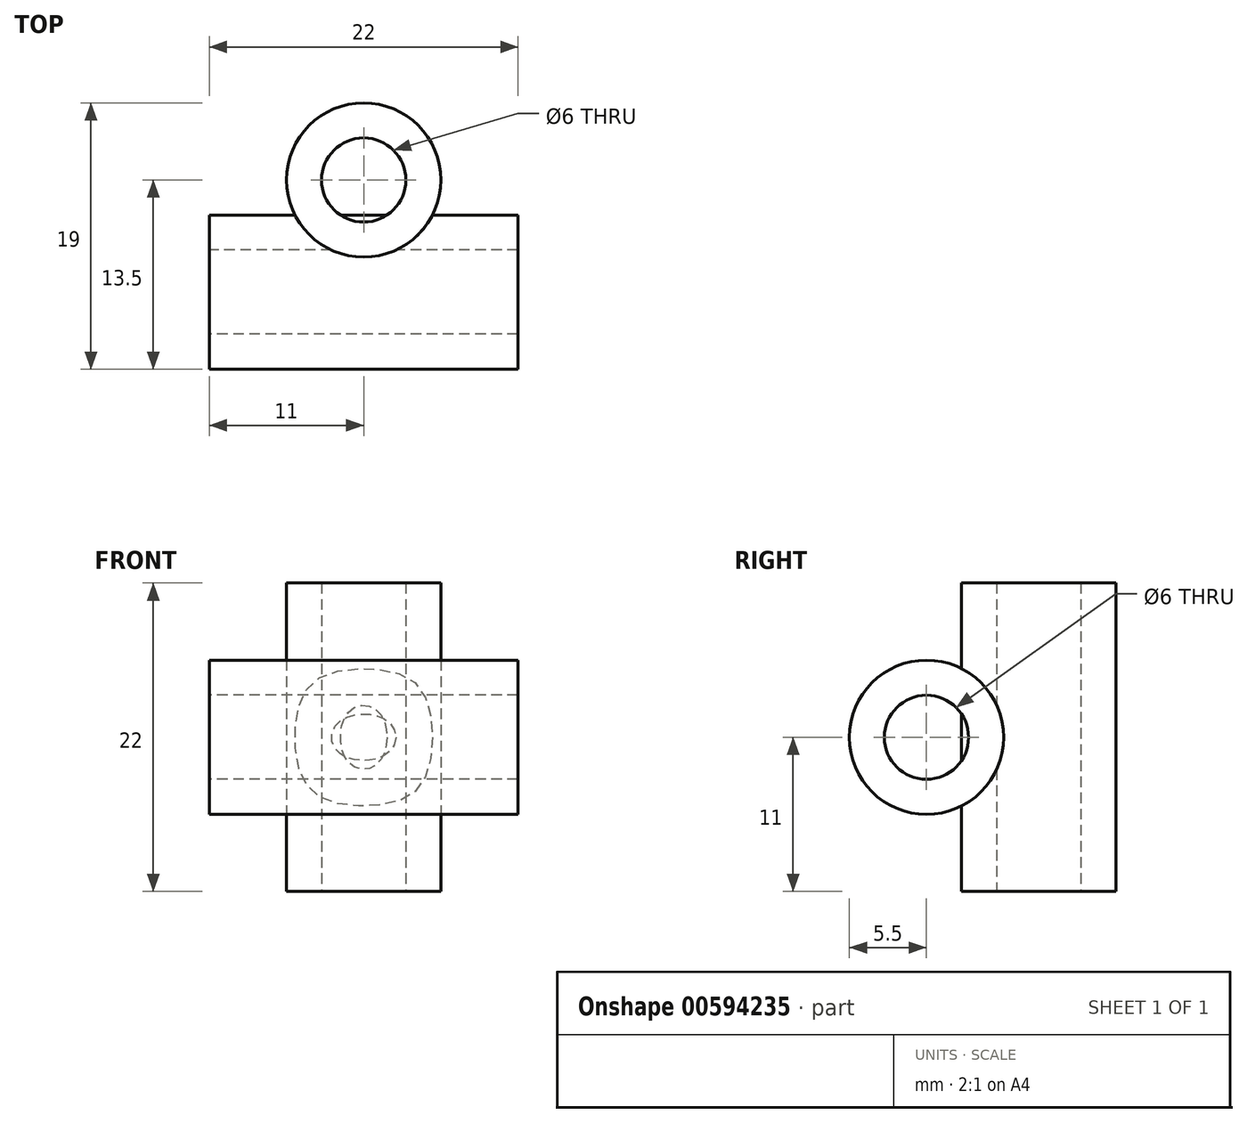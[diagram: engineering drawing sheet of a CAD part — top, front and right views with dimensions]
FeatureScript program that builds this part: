
annotation { "Feature Type Name" : "Feature", "Feature Type Description" : "" }
export const myFeature = defineFeature(function(context is Context, id is Id, definition is map)
    precondition{}
    {
        {
            var Q0;
            Q0=qCreatedBy(makeId("Right.planeOp"),FACE);
            var sketch = newSketch(context, id + "F0", { "sketchPlane" : qUnion([Q0])});
            skCircle(sketch, "E0", {"center": v(0, 0) * mm, "radius": 5.5 * mm});
            skCircle(sketch, "E1", {"center": v(0, 0) * mm, "radius": 3 * mm});
            skSolve(sketch);
        }
        {
            var Q0;
            Q0 = qSketchRegion(id + "F0", true);
            extrude(context, id + "F1", {"entities" : qUnion([Q0]), "endBound" : BoundingType.SYMMETRIC, "depth" : 22 * mm, "offsetDistance" : 25.4 * mm});
        }
        {
            var Q0;
            Q0=qCreatedBy(makeId("Top.planeOp"),FACE);
            var sketch = newSketch(context, id + "F2", { "sketchPlane" : qUnion([Q0])});
            skCircle(sketch, "E2", {"center": v(0, 8) * mm, "radius": 5.5 * mm});
            skCircle(sketch, "E3", {"center": v(0, 8) * mm, "radius": 3 * mm});
            skSolve(sketch);
        }
        {
            var Q0;
            Q0 = qSketchRegion(id + "F2", true);
            extrude(context, id + "F3", {"entities" : qUnion([Q0]), "operationType" : NewBodyOperationType.ADD, "endBound" : BoundingType.SYMMETRIC, "depth" : 22 * mm, "offsetDistance" : 25.4 * mm});
        }
    });
